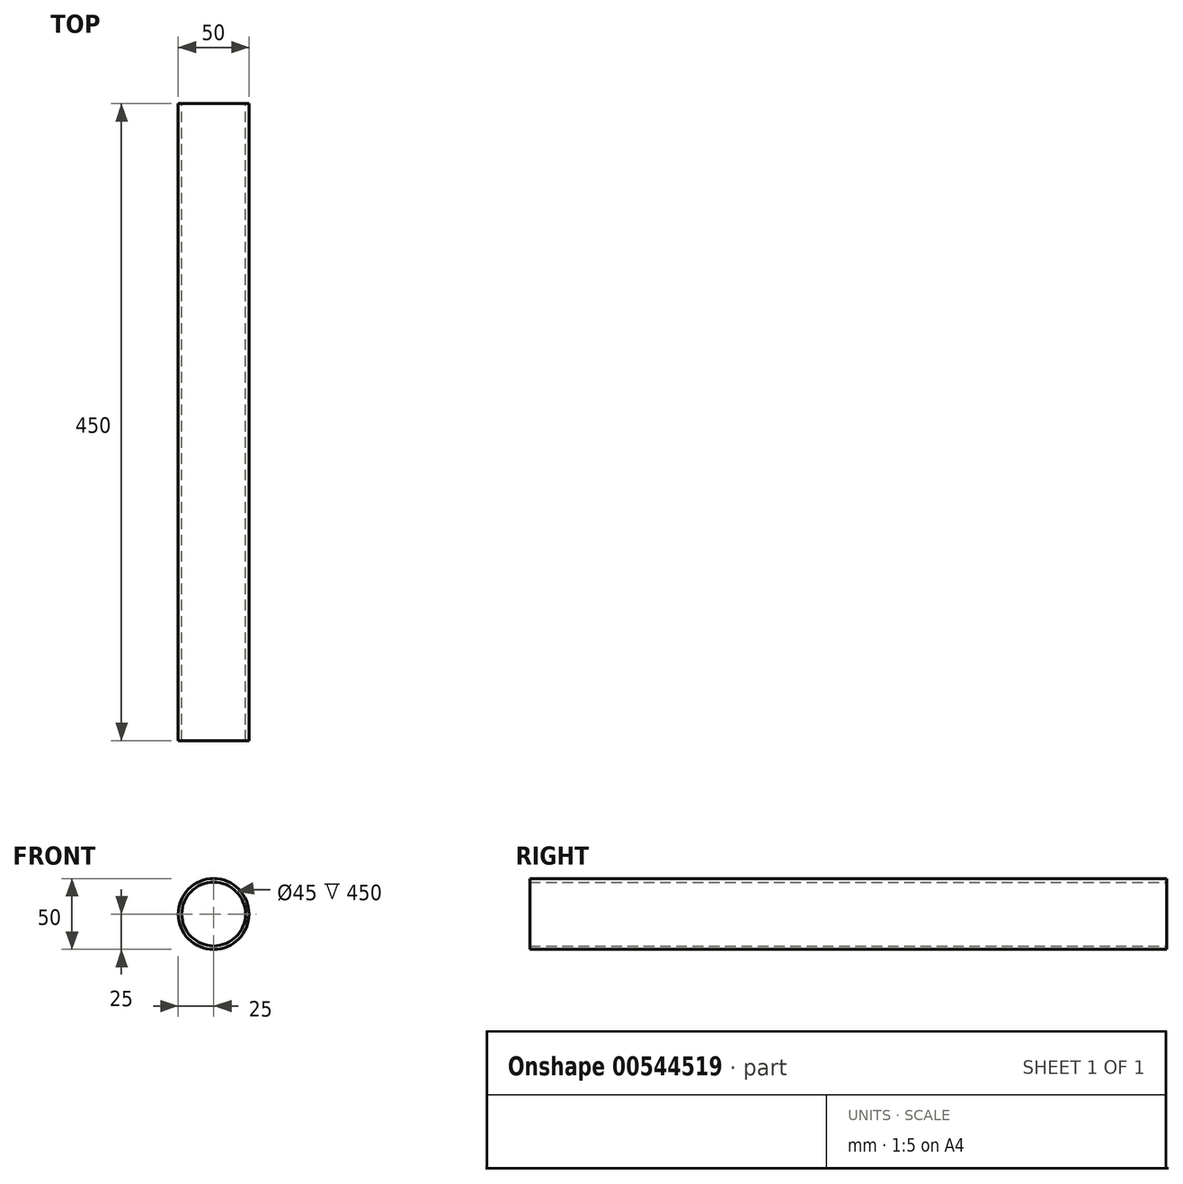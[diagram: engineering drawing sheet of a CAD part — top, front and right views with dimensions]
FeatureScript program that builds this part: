
annotation { "Feature Type Name" : "Feature", "Feature Type Description" : "" }
export const myFeature = defineFeature(function(context is Context, id is Id, definition is map)
    precondition{}
    {
        {
            var Q0;
            Q0=qCreatedBy(makeId("Front.planeOp"),FACE);
            var sketch = newSketch(context, id + "F0", { "sketchPlane" : qUnion([Q0])});
            skCircle(sketch, "E0", {"center": v(0, 0) * mm, "radius": 22.5 * mm});
            skCircle(sketch, "E1", {"center": v(0, 0) * mm, "radius": 25 * mm});
            skSolve(sketch);
        }
        {
            var Q0;
            Q0=makeQuery(id+"F0.imprint","IMPRINT",FACE,{"disambiguationData":[TD([[makeQuery(id+"F0.imprint","IMPRINT",EDGE,{"derivedFrom":sQuery(id+"F0.wireOp",EDGE,"E0")}),-1.0]])]});
            extrude(context, id + "F1", {"entities" : qUnion([Q0]), "depth" : 450 * mm, "offsetDistance" : 25 * mm});
        }
    });
